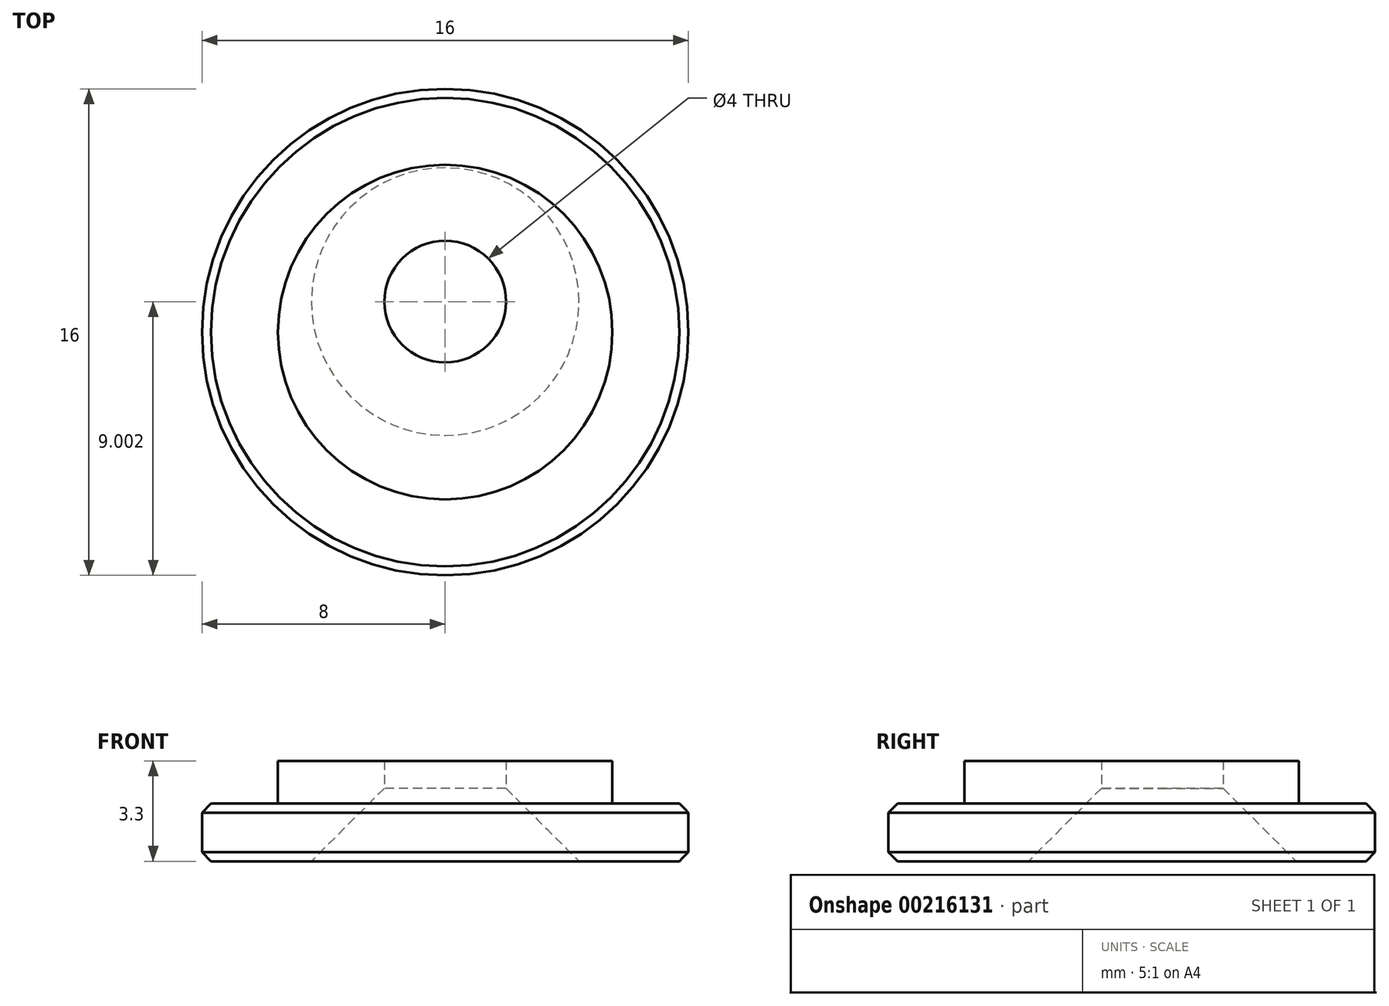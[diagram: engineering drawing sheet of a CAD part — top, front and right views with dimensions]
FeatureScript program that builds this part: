
annotation { "Feature Type Name" : "Feature", "Feature Type Description" : "" }
export const myFeature = defineFeature(function(context is Context, id is Id, definition is map)
    precondition{}
    {
        {
            var Q0;
            Q0=qCreatedBy(makeId("Top.planeOp"),FACE);
            var sketch = newSketch(context, id + "F0", { "sketchPlane" : qUnion([Q0])});
            skCircle(sketch, "E0", {"center": v(0, -2) * mm, "radius": 5.5 * mm});
            skCircle(sketch, "E1", {"center": v(0, -2) * mm, "radius": 8 * mm});
            skCircle(sketch, "E2", {"center": v(0, -1) * mm, "radius": 2 * mm});
            skSolve(sketch);
        }
        {
            var Q0;
            Q0=makeQuery(id+"F0.imprint","IMPRINT",FACE,{"disambiguationData":[TD([[makeQuery(id+"F0.imprint","IMPRINT",EDGE,{"derivedFrom":sQuery(id+"F0.wireOp",EDGE,"0sNOU6fx-ZL20-ZjI8-KMeZ-MdryJRZQKmVk")}),-1.0]])]});
            var Q1;
            Q1=makeQuery(id+"F0.imprint","IMPRINT",FACE,{"disambiguationData":[TD([[makeQuery(id+"F0.imprint","IMPRINT",EDGE,{"derivedFrom":sQuery(id+"F0.wireOp",EDGE,"E0")}),1.0]])]});
            var Q2;
            Q2=sQuery(id+"F0.wireOp",EDGE,"0sNOU6fx-ZL20-ZjI8-KMeZ-MdryJRZQKmVk");
            var Q3;
            Q3=sQuery(id+"F0.wireOp",EDGE,"E0");
            extrude(context, id + "F1", {"entities" : qUnion([Q0, Q1]), "surfaceEntities" : qUnion([Q2, Q3]), "depth" : 3.3 * mm});
        }
        {
            var Q0;
            Q0 = qSketchRegion(id + "F0", true);
            extrude(context, id + "F2", {"entities" : qUnion([Q0]), "operationType" : NewBodyOperationType.ADD, "depth" : 1.9 * mm});
        }
        {
            var Q0;
            Q0=makeQuery(id+"F1.opExtrude","CAP_EDGE",EDGE,{"disambiguationData":[OSD([sQuery(id+"F0.wireOp",EDGE,"E2")])],"isStart":true});
            chamfer(context, id + "F3", {"entities" : qUnion([Q0]), "width" : 2.4 * mm, "tangentPropagation" : true});
        }
        {
            var Q0;
            Q0=makeQuery(id+"F2.opExtrude","CAP_EDGE",EDGE,{"disambiguationData":[OSD([sQuery(id+"F0.wireOp",EDGE,"E1")])],"isStart":false});
            var Q1;
            Q1=makeQuery(id+"F2.opExtrude","CAP_EDGE",EDGE,{"disambiguationData":[OSD([sQuery(id+"F0.wireOp",EDGE,"E1")])],"isStart":true});
            chamfer(context, id + "F4", {"entities" : qUnion([Q0, Q1]), "width" : 0.3 * mm, "tangentPropagation" : true});
        }
    });
